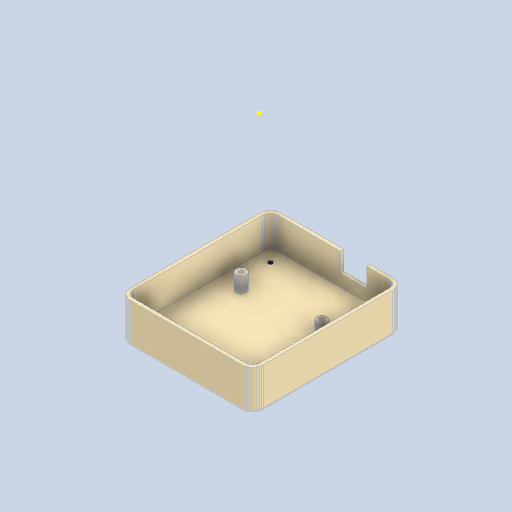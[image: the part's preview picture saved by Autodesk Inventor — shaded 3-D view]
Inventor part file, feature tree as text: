
AUTODESK INVENTOR PART (.ipt)
format: ipt  version: 2022.1 (Build 261234000, 234)  size: 1,032,192 bytes
history: native  units: mm
features: sketch x5, hole x4, other x3
ambient origin geometry x8: Origin, YZ Plane, XZ Plane, XY Plane, X Axis, Y Axis, Z Axis, Center Point
bodies: Body1 (feature_tree)
feature tree (12):
  other  "Sólido1"
  other  "nucleo-case-base"
  other  "MeshFeature1"
  hole  "Agujero1"  [1 undecoded]
  hole  "Agujero2"  [1 undecoded]
  hole  "Agujero3"  [1 undecoded]
  hole  "Agujero4"  [1 undecoded]
  sketch  "Boceto7"  dims[d19=10.0mm d20=3.0mm d21=6.0mm d22=4.0mm d23=2.0mm d24=90.0deg d25=8.0mm d26=20.594885mm d27=10.0mm d28=10.0mm d29=3.0mm d30=6.0mm d31=4.0mm d32=2.0mm d33=90.0deg d34=8.0mm d35=20.594885mm d36=0.5mm d37=0.872665mm d38=0.5mm d39=0.872665mm d40=0.5mm d41=0.872665mm]
  sketch  "Boceto1"  dims[d0=10.0mm d1=10.0mm]
  sketch  "Boceto2"  dims[d2=3.0mm d3=6.0mm d4=4.0mm d5=2.0mm d6=90.0deg d7=8.0mm d8=20.594885mm d9=10.0mm]
  sketch  "Boceto3"  dims[d10=10.0mm]
  sketch  "Boceto4"  dims[d11=3.0mm d12=6.0mm d13=4.0mm d14=2.0mm d15=90.0deg d16=8.0mm d17=20.594885mm d18=10.0mm]
note: 4 required parameter values undecoded (feature->parameter linkage not recoverable at this tier; creation-order binding heuristic only, values carry confidence <= 0.55)
